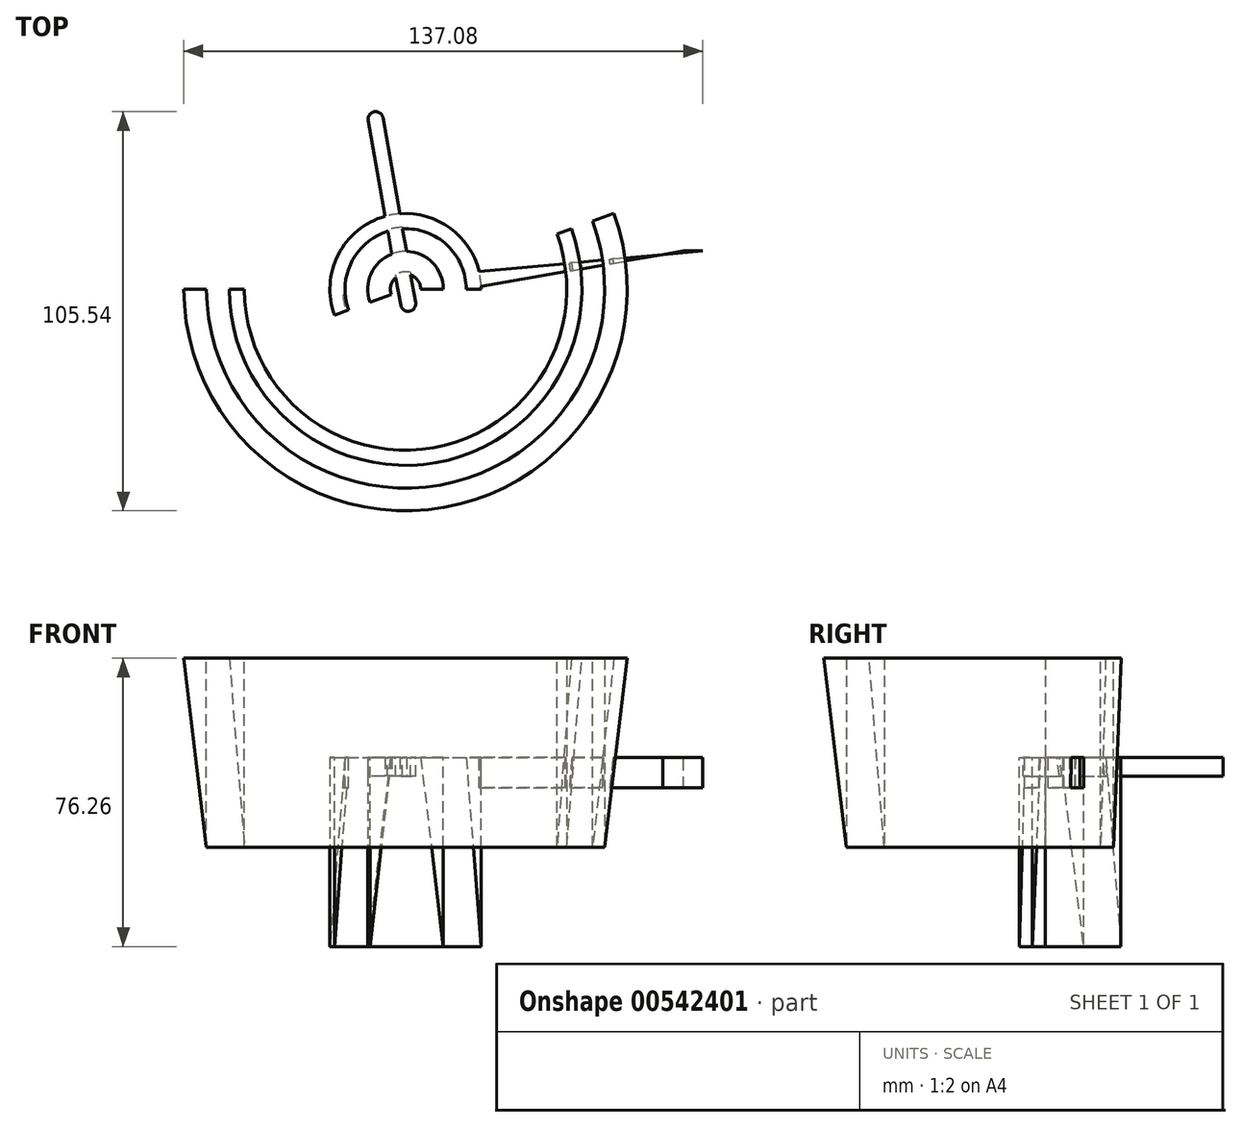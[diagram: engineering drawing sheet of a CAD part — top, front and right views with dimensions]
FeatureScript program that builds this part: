
annotation { "Feature Type Name" : "Feature", "Feature Type Description" : "" }
export const myFeature = defineFeature(function(context is Context, id is Id, definition is map)
    precondition{}
    {
        {
            var Q0;
            Q0=qCreatedBy(makeId("Top.planeOp"),FACE);
            var sketch = newSketch(context, id + "F0", { "sketchPlane" : qUnion([Q0])});
            skArc(sketch, "E0", {"start": v(20, 0) * mm, "mid": v(0, 20) * mm, "end": v(-20, 0) * mm});
            skSolve(sketch);
        }
        {
            var Q0;
            Q0=qCreatedBy(makeId("Front.planeOp"),FACE);
            var sketch = newSketch(context, id + "F1", { "sketchPlane" : qUnion([Q0])});
            skLineSegment(sketch, "E1", {"start": v(20, 0) * mm, "end": v(20, 50) * mm});
            skLineSegment(sketch, "E2", {"start": v(20, 50) * mm, "end": v(16, 50) * mm});
            skLineSegment(sketch, "E3", {"start": v(16, 50) * mm, "end": v(20, 0) * mm});
            skLineSegment(sketch, "E4", {"start": v(0, 0) * mm, "end": v(0, 110.06) * mm});
            skLineSegment(sketch, "E5", {"start": v(0, 0) * mm, "end": v(20, 0) * mm});
            skLineSegment(sketch, "E6", {"start": v(10, 0) * mm, "end": v(10, 50) * mm});
            skLineSegment(sketch, "E7", {"start": v(10, 50) * mm, "end": v(4, 50) * mm});
            skLineSegment(sketch, "E8", {"start": v(4, 50) * mm, "end": v(10, 0) * mm});
            skLineSegment(sketch, "E9", {"start": v(-42.6, 26.26) * mm, "end": v(-42.6, 76.26) * mm});
            skLineSegment(sketch, "E10", {"start": v(-42.6, 76.26) * mm, "end": v(-46.6, 76.26) * mm});
            skLineSegment(sketch, "E11", {"start": v(-46.6, 76.26) * mm, "end": v(-42.6, 26.26) * mm});
            skLineSegment(sketch, "E12", {"start": v(-93.23, 26.26) * mm, "end": v(-42.6, 26.26) * mm});
            skLineSegment(sketch, "E13", {"start": v(-52.6, 26.26) * mm, "end": v(-52.6, 76.26) * mm});
            skLineSegment(sketch, "E14", {"start": v(-52.6, 76.26) * mm, "end": v(-58.6, 76.26) * mm});
            skLineSegment(sketch, "E15", {"start": v(-58.6, 76.26) * mm, "end": v(-52.6, 26.26) * mm});
            skSolve(sketch);
        }
        {
            var Q0;
            Q0 = qSketchRegion(id + "F1", true);
            var Q1;
            Q1=sQuery(id+"F1.wireOp",EDGE,"E4");
            revolve(context, id + "F2", {"entities" : qUnion([Q0]), "axis" : qUnion([Q1]), "revolveType" : RevolveType.ONE_DIRECTION, "angle" : 200 * degree});
        }
        {
            var Q0;
            Q0=makeQuery(id+"F2.opRevolve","SWEPT_FACE",FACE,{"disambiguationData":[OSD([sQuery(id+"F1.wireOp",EDGE,"E2")])]});
            var sketch = newSketch(context, id + "F3", { "sketchPlane" : qUnion([Q0])});
            skLineSegment(sketch, "E16", {"start": v(-15.04, -5.47) * mm, "end": v(73.48, 10.14) * mm});
            skLineSegment(sketch, "E17", {"start": v(73.48, 10.14) * mm, "end": v(78.48, 10.14) * mm});
            skLineSegment(sketch, "E18", {"start": v(78.48, 10.14) * mm, "end": v(19.45, 4.67) * mm});
            skLineSegment(sketch, "E19", {"start": v(19.45, 4.67) * mm, "end": v(-19.87, -2.26) * mm});
            skLineSegment(sketch, "E20", {"start": v(-19.87, -2.26) * mm, "end": v(-18.8, -6.84) * mm});
            skLineSegment(sketch, "E21", {"start": v(-18.8, -6.84) * mm, "end": v(-15.04, -5.47) * mm});
            skSolve(sketch);
        }
        {
            var Q0;
            {var subQ0=sQuery(id+"F3.wireOp",EDGE,"E16");Q0=makeQuery(id+"F3.imprint","IMPRINT",FACE,{"disambiguationData":[TD([[makeQuery(id+"F3.imprint","IMPRINT",EDGE,{"derivedFrom":subQ0}),1.0]])]});}
            var Q1;
            {var subQ0=sQuery(id+"F3.wireOp",EDGE,"E20");Q1=makeQuery(id+"F3.imprint","IMPRINT",FACE,{"disambiguationData":[TD([[makeQuery(id+"F3.imprint","IMPRINT",EDGE,{"derivedFrom":subQ0}),1.0]])]});}
            var Q2;
            {var subQ0=sQuery(id+"F3.wireOp",EDGE,"E17");Q2=makeQuery(id+"F3.imprint","IMPRINT",FACE,{"disambiguationData":[TD([[makeQuery(id+"F3.imprint","IMPRINT",EDGE,{"derivedFrom":subQ0}),-1.0]])]});}
            extrude(context, id + "F4", {"entities" : qUnion([Q0, Q1, Q2]), "operationType" : NewBodyOperationType.ADD, "depth" : 0 * mm, "offsetDistance" : 25 * mm, "hasSecondDirection" : true, "secondDirectionOppositeDirection" : true, "secondDirectionDepth" : 8 * mm});
        }
        {
            var Q0;
            {var subQ0=makeQuery(id+"F2.opRevolve","SWEPT_FACE",FACE,{"disambiguationData":[OSD([sQuery(id+"F1.wireOp",EDGE,"E2")])]});Q0=makeQuery(id+"F4.boolean.opBoolean","SPLIT",FACE,{"disambiguationData":[TD([makeQuery(id+"F2.opRevolve","SWEPT_FACE",FACE,{"disambiguationData":[OSD([sQuery(id+"F1.wireOp",EDGE,"E3")])]})])],"derivedFrom":subQ0});}
            var sketch = newSketch(context, id + "F5", { "sketchPlane" : qUnion([Q0])});
            skLineSegment(sketch, "E22", {"start": v(-2.54, -4.43) * mm, "end": v(3.9, -3.3) * mm});
            skLineSegment(sketch, "E23", {"start": v(0, 0) * mm, "end": v(0.68, -3.86) * mm});
            skLineSegment(sketch, "E24", {"start": v(0.68, -3.86) * mm, "end": v(0, 0) * mm});
            skLineSegment(sketch, "E25", {"start": v(2.78, -15.76) * mm, "end": v(0.68, -3.86) * mm});
            skLineSegment(sketch, "E26.0", {"start": v(-1.29, -4.21) * mm, "end": v(-9.9, 44.6) * mm});
            skLineSegment(sketch, "E27.0", {"start": v(2.65, -3.52) * mm, "end": v(-5.95, 45.3) * mm});
            skArc(sketch, "E28", {"start": v(-5.95, 45.3) * mm, "mid": v(-8.27, 46.91) * mm, "end": v(-9.9, 44.6) * mm});
            skArc(sketch, "E29", {"start": v(-1.29, -4.21) * mm, "mid": v(1.03, -5.83) * mm, "end": v(2.65, -3.52) * mm});
            skSolve(sketch);
        }
        {
            var Q0;
            Q0 = qSketchRegion(id + "F5", true);
            extrude(context, id + "F6", {"entities" : qUnion([Q0]), "operationType" : NewBodyOperationType.ADD, "depth" : 0 * mm, "offsetDistance" : 25 * mm, "hasSecondDirection" : true, "secondDirectionOppositeDirection" : true, "secondDirectionDepth" : 5 * mm});
        }
    });
